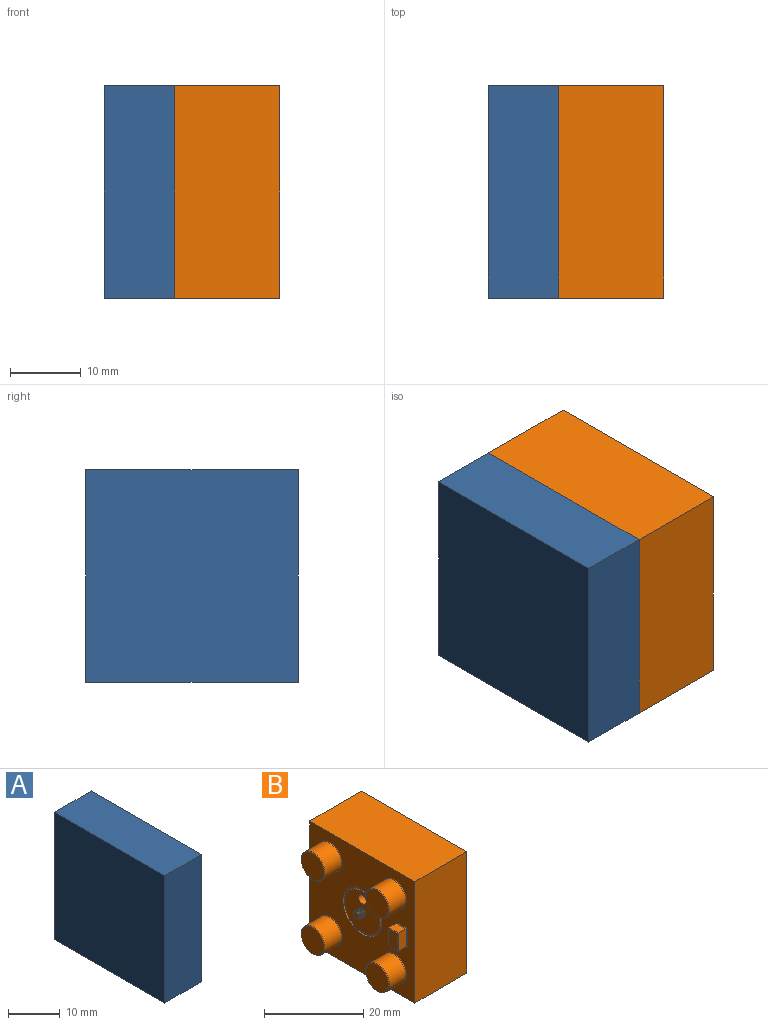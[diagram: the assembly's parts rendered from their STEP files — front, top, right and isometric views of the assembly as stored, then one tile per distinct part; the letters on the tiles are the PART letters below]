
ASSEMBLY  parts=2 mates=1
PART A: 47 faces, bbox 10.2x30x30 mm
  f0: plane 30x30mm, normal (1,0,0), area 635mm2, adj f14,f15,f19,f21,f22,f23,f24,f29
  f1: cylinder r=3.35mm len=6.69mm, axis (1,0,0), area 98.8mm2, adj f15,f16
  f2: plane 6.39x6.39mm, normal (1,0,0), area 32.1mm2, adj f16
  f3: cylinder r=3.35mm len=6.69mm, axis (1,0,0), area 98.8mm2, adj f14,f17
  f4: plane 6.39x6.39mm, normal (1,0,0), area 32.1mm2, adj f17
  f5: cylinder r=3.35mm len=6.69mm, axis (1,0,0), area 98.8mm2, adj f18,f29
  f6: plane 6.39x6.39mm, normal (1,0,0), area 32.1mm2, adj f18
  f7: cylinder r=3.35mm len=6.69mm, axis (1,0,0), area 98.8mm2, adj f19,f20
  f8: plane 6.39x6.39mm, normal (1,0,0), area 32.1mm2, adj f20
  f9: plane 2.75x2.2mm, normal (0,0,-1), area 6.1mm2, adj f10,f12,f21,f26
  f10: plane 4.5x2.2mm, normal (0,-1,0), area 9.9mm2, adj f9,f11,f22,f25
  f11: plane 2.75x2.2mm, normal (0,0,1), area 6.1mm2, adj f10,f12,f24,f27
  f12: plane 4.5x2.2mm, normal (0,1,0), area 9.9mm2, adj f9,f11,f23,f28
  f13: plane 4.2x2.45mm, normal (1,0,0), area 10.3mm2, adj f25,f26,f27,f28
  f14: torus R=3.5mm, axis (-1,0,0), area 5mm2, adj f0,f3
  f15: torus R=3.5mm, axis (-1,0,0), area 5mm2, adj f0,f1
  f16: torus R=3.2mm, axis (-1,0,0), area 4.9mm2, adj f1,f2
  f17: torus R=3.2mm, axis (-1,0,0), area 4.9mm2, adj f3,f4
  f18: torus R=3.2mm, axis (-1,0,0), area 4.9mm2, adj f5,f6
  f19: torus R=3.5mm, axis (-1,0,0), area 5mm2, adj f0,f7
  f20: torus R=3.2mm, axis (-1,0,0), area 4.9mm2, adj f7,f8
  f21: cylinder r=0.15mm len=3.05mm, axis (0,-1,0), area 0.7mm2, adj f0,f9,f22,f23
  f22: cylinder r=0.15mm len=4.8mm, axis (0,0,1), area 1.1mm2, adj f0,f10,f21,f24
  f23: cylinder r=0.15mm len=4.8mm, axis (0,0,-1), area 1.1mm2, adj f0,f12,f21,f24
  f24: cylinder r=0.15mm len=3.05mm, axis (0,1,0), area 0.7mm2, adj f0,f11,f22,f23
  f25: cylinder r=0.15mm len=4.5mm, axis (0,0,-1), area 1mm2, adj f10,f13,f26,f27
  f26: cylinder r=0.15mm len=2.75mm, axis (0,1,0), area 0.6mm2, adj f9,f13,f25,f28
  f27: cylinder r=0.15mm len=2.75mm, axis (0,-1,0), area 0.6mm2, adj f11,f13,f25,f28
  f28: cylinder r=0.15mm len=4.5mm, axis (0,0,1), area 1mm2, adj f12,f13,f26,f27
  f29: torus R=3.5mm, axis (-1,0,0), area 5mm2, adj f0,f5
  f30: cylinder r=2.23mm len=4.45mm, axis (-1,0,0), area 3.5mm2, adj f31,f41
  f31: plane 4.81x4.81mm, normal (1,0,0), area 2.6mm2, adj f30,f32
  f32: cylinder r=2.4mm len=4.81mm, axis (-1,0,0), area 3.8mm2, adj f31,f33
  f33: cone r=2.62mm half-angle=7.4deg, axis (-1,0,0), area 26.6mm2, adj f32,f34
  f34: torus R=3.11mm, axis (-1,0,0), area 17.5mm2, adj f33,f35
  f35: torus R=3.04mm, axis (-1,0,0), area 16.5mm2, adj f34,f36
  f36: cone r=3.67mm half-angle=2.9deg, axis (-1,0,0), area 15.2mm2, adj f35,f37
  f37: torus R=4.21mm, axis (-1,0,0), area 55.5mm2, adj f36,f38
  f38: plane 10.1x10.1mm, normal (1,0,0), area 24.4mm2, adj f37,f40
  f39: cylinder r=5.55mm len=11.1mm, axis (-1,0,0), area 6.5mm2, adj f0,f40
  f40: torus R=5.05mm, axis (1,0,0), area 26.5mm2, adj f38,f39
  f41: plane 4.45x4.45mm, normal (1,0,0), area 15.6mm2, adj f30
  f42: plane 30x10mm, normal (0,1,0), area 300mm2, adj f0,f43,f45,f46
  f43: plane 30x10mm, normal (0,0,1), area 300mm2, adj f0,f42,f44,f46
  f44: plane 30x10mm, normal (0,-1,0), area 300mm2, adj f0,f43,f45,f46
  f45: plane 30x10mm, normal (0,0,-1), area 300mm2, adj f0,f42,f44,f46
  f46: plane 30x30mm, normal (-1,0,0), area 900mm2, adj f42,f43,f44,f45
PART B: 49 faces, bbox 20x30.2x30.2 mm
  f0: plane 30x30mm, normal (-1,0,0), area 635mm2, adj f3,f4,f5,f6,f20,f21,f25,f27
  f1: cylinder r=1.12mm len=14.83mm, axis (-1,0,0), area 104.8mm2, adj f2,f48
  f2: plane 30x30mm, normal (1,0,0), area 896mm2, adj f1,f3,f4,f5,f6
  f3: plane 30x14.83mm, normal (0,0,-1), area 444.9mm2, adj f0,f2,f5,f6
  f4: plane 30x14.83mm, normal (0,0,1), area 444.9mm2, adj f0,f2,f5,f6
  f5: plane 30x14.83mm, normal (0,-1,0), area 444.9mm2, adj f0,f2,f3,f4
  f6: plane 30x14.83mm, normal (0,1,0), area 444.9mm2, adj f0,f2,f3,f4
  f7: cylinder r=3.35mm len=6.69mm, axis (1,0,0), area 98.8mm2, adj f21,f22
  f8: plane 6.39x6.39mm, normal (-1,0,0), area 32.1mm2, adj f22
  f9: cylinder r=3.35mm len=6.69mm, axis (1,0,0), area 98.8mm2, adj f20,f23
  f10: plane 6.39x6.39mm, normal (-1,0,0), area 32.1mm2, adj f23
  f11: cylinder r=3.35mm len=6.69mm, axis (1,0,0), area 98.8mm2, adj f24,f35
  f12: plane 6.39x6.39mm, normal (-1,0,0), area 32.1mm2, adj f24
  f13: cylinder r=3.35mm len=6.69mm, axis (1,0,0), area 98.8mm2, adj f25,f26
  f14: plane 6.39x6.39mm, normal (-1,0,0), area 32.1mm2, adj f26
  f15: plane 2.75x2.2mm, normal (0,0,1), area 6.1mm2, adj f16,f18,f27,f32
  f16: plane 4.5x2.2mm, normal (0,1,0), area 9.9mm2, adj f15,f17,f28,f31
  f17: plane 2.75x2.2mm, normal (0,0,-1), area 6.1mm2, adj f16,f18,f30,f33
  f18: plane 4.5x2.2mm, normal (0,-1,0), area 9.9mm2, adj f15,f17,f29,f34
  f19: plane 4.2x2.45mm, normal (-1,0,0), area 10.3mm2, adj f31,f32,f33,f34
  f20: torus R=3.5mm, axis (-1,0,0), area 5mm2, adj f0,f9
  f21: torus R=3.5mm, axis (-1,0,0), area 5mm2, adj f0,f7
  f22: torus R=3.2mm, axis (-1,0,0), area 4.9mm2, adj f7,f8
  f23: torus R=3.2mm, axis (-1,0,0), area 4.9mm2, adj f9,f10
  f24: torus R=3.2mm, axis (-1,0,0), area 4.9mm2, adj f11,f12
  f25: torus R=3.5mm, axis (-1,0,0), area 5mm2, adj f0,f13
  f26: torus R=3.2mm, axis (-1,0,0), area 4.9mm2, adj f13,f14
  f27: cylinder r=0.15mm len=3.05mm, axis (0,-1,0), area 0.7mm2, adj f0,f15,f28,f29
  f28: cylinder r=0.15mm len=4.8mm, axis (0,0,1), area 1.1mm2, adj f0,f16,f27,f30
  f29: cylinder r=0.15mm len=4.8mm, axis (0,0,-1), area 1.1mm2, adj f0,f18,f27,f30
  f30: cylinder r=0.15mm len=3.05mm, axis (0,1,0), area 0.7mm2, adj f0,f17,f28,f29
  f31: cylinder r=0.15mm len=4.5mm, axis (0,0,-1), area 1mm2, adj f16,f19,f32,f33
  f32: cylinder r=0.15mm len=2.75mm, axis (0,1,0), area 0.6mm2, adj f15,f19,f31,f34
  f33: cylinder r=0.15mm len=2.75mm, axis (0,-1,0), area 0.6mm2, adj f17,f19,f31,f34
  f34: cylinder r=0.15mm len=4.5mm, axis (0,0,1), area 1mm2, adj f18,f19,f32,f33
  f35: torus R=3.5mm, axis (-1,0,0), area 5mm2, adj f0,f11
  f36: cylinder r=5.55mm len=11.1mm, axis (-1,0,0), area 12.2mm2, adj f0,f40
  f37: plane 10.8x10.8mm, normal (-1,0,0), area 6.7mm2, adj f39,f40
  f38: cylinder r=5.05mm len=10.1mm, axis (-1,0,0), area 11.1mm2, adj f39,f48
  f39: torus R=5.2mm, axis (1,0,0), area 7.6mm2, adj f37,f38
  f40: torus R=5.4mm, axis (1,0,0), area 8.1mm2, adj f36,f37
  f41: plane 1.4x1.4mm, normal (-1,0,0), area 1.5mm2, adj f42
  f42: cone r=1mm half-angle=45deg, axis (1,0,0), area 1mm2, adj f41,f43,f44,f47
  f43: cone r=1mm half-angle=45deg, axis (1,0,0), area 0.3mm2, adj f42,f45,f46,f47
  f44: cylinder r=0.74mm len=1.76mm, axis (1,0,0), area 1mm2, adj f42,f45,f47,f48
  f45: bspline ~2.3x2.08mm, area 6.7mm2, adj f43,f44,f46,f48
  f46: cylinder r=1mm len=2mm, axis (-1,0,0), area 1mm2, adj f43,f45,f47,f48
  f47: bspline ~2.3x2.15mm, area 6.7mm2, adj f42,f43,f44,f46,f48
  f48: plane 10.26x10.26mm, normal (-1,0,0), area 73.7mm2, adj f1,f38,f44,f45,f46,f47
PLACE A at identity
PLACE B at identity
MATE slider B.f7 <-> A.f1  axis (-1,0,0) through (-3.27,9.2,9.18)mm
